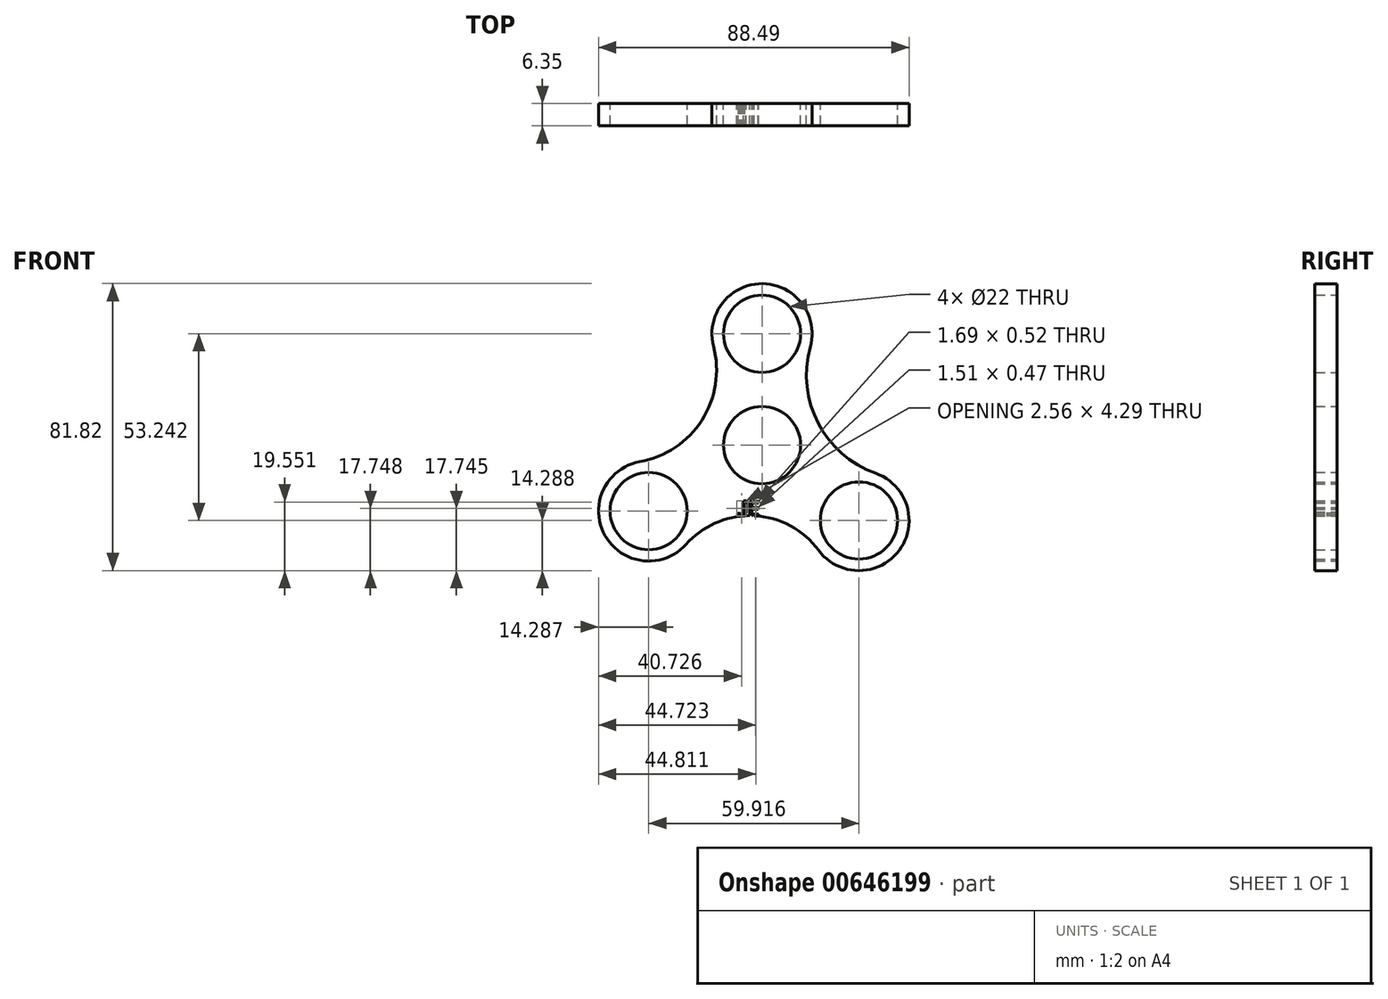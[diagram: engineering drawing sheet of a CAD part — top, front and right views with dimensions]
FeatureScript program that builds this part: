
annotation { "Feature Type Name" : "Feature", "Feature Type Description" : "" }
export const myFeature = defineFeature(function(context is Context, id is Id, definition is map)
    precondition{}
    {
        {
            var Q0;
            Q0=qCreatedBy(makeId("Front.planeOp"),FACE);
            var sketch = newSketch(context, id + "F0", { "sketchPlane" : qUnion([Q0])});
            skCircle(sketch, "E0", {"center": v(0, 0) * mm, "radius": 11 * mm});
            skCircle(sketch, "E1", {"center": v(0, 0) * mm, "radius": 14.29 * mm});
            skCircle(sketch, "E2", {"center": v(0, 31.75) * mm, "radius": 11 * mm});
            skCircle(sketch, "E3", {"center": v(0, 31.75) * mm, "radius": 14.29 * mm});
            skCircle(sketch, "E4.1.0", {"center": v(-32.3, -18.79) * mm, "radius": 14.29 * mm});
            skCircle(sketch, "E4.1.1", {"center": v(-32.3, -18.79) * mm, "radius": 11 * mm});
            skCircle(sketch, "E4.2.0", {"center": v(27.61, -21.5) * mm, "radius": 14.29 * mm});
            skCircle(sketch, "E4.2.1", {"center": v(27.61, -21.5) * mm, "radius": 11 * mm});
            skPoint(sketch, "E4.center", {"position": v(-1.56, -2.84) * mm});
            skArc(sketch, "E5", {"start": v(-34.83, -4.72) * mm, "mid": v(-17.14, 7.12) * mm, "end": v(-13.82, 28.14) * mm});
            skArc(sketch, "E6", {"start": v(13.76, 27.9) * mm, "mid": v(16, 6.26) * mm, "end": v(32.4, -8.03) * mm});
            skArc(sketch, "E7", {"start": v(16.13, -29.99) * mm, "mid": v(-2.35, -20.15) * mm, "end": v(-21.63, -28.28) * mm});
            skText(sketch, "E8", { "text": "JE", "fontName": "AllertaStencil-Regular.ttf"});
            skPoint(sketch, "E8.secondSnap0", {"position": v(-2.35, -20.15) * mm});
            const initialGuessF0  = {"E8": [-0.00729, -0.02015, 1, 0, 0.00418]};
            skSetInitialGuess(sketch, initialGuessF0);
            skSolve(sketch);
        }
        {
            var Q0;
            Q0=makeQuery(id+"F0.imprint","IMPRINT",FACE,{"disambiguationData":[TD([[makeQuery(id+"F0.imprint","IMPRINT",EDGE,{"derivedFrom":sQuery(id+"F0.wireOp",EDGE,"E2")}),-1.0]])]});
            var Q1;
            Q1=makeQuery(id+"F0.imprint","IMPRINT",FACE,{"disambiguationData":[TD([[makeQuery(id+"F0.imprint","IMPRINT",EDGE,{"derivedFrom":sQuery(id+"F0.wireOp",EDGE,"E1")}),-1.0]])]});
            var Q2;
            Q2=makeQuery(id+"F0.imprint","IMPRINT",FACE,{"disambiguationData":[TD([[makeQuery(id+"F0.imprint","IMPRINT",EDGE,{"derivedFrom":sQuery(id+"F0.wireOp",EDGE,"E0")}),-1.0]])]});
            var Q3;
            Q3=makeQuery(id+"F0.imprint","IMPRINT",FACE,{"disambiguationData":[TD([[makeQuery(id+"F0.imprint","IMPRINT",EDGE,{"derivedFrom":sQuery(id+"F0.wireOp",EDGE,"E4.2.1")}),-1.0]])]});
            var Q4;
            Q4=makeQuery(id+"F0.imprint","IMPRINT",FACE,{"disambiguationData":[TD([[makeQuery(id+"F0.imprint","IMPRINT",EDGE,{"derivedFrom":sQuery(id+"F0.wireOp",EDGE,"E4.1.1")}),-1.0]])]});
            extrude(context, id + "F1", {"entities" : qUnion([Q0, Q1, Q2, Q3, Q4]), "depth" : 6.35 * mm, "offsetDistance" : 25.4 * mm});
        }
    });
